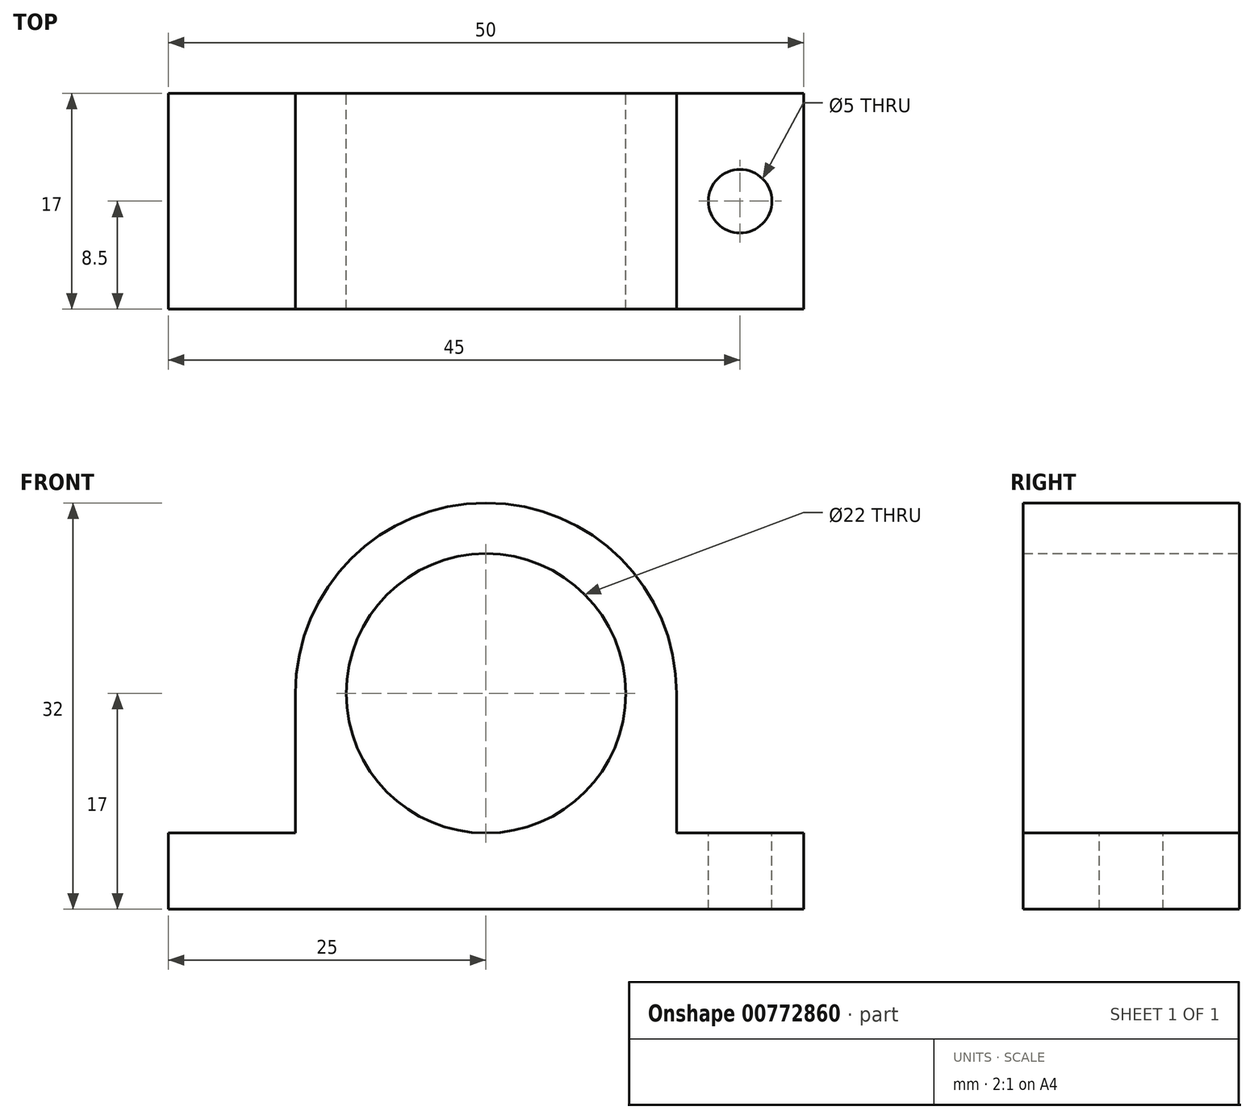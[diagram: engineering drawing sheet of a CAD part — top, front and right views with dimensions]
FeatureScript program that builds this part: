
annotation { "Feature Type Name" : "Feature", "Feature Type Description" : "" }
export const myFeature = defineFeature(function(context is Context, id is Id, definition is map)
    precondition{}
    {
        {
            var Q0;
            Q0=qCreatedBy(makeId("Front.planeOp"),FACE);
            var sketch = newSketch(context, id + "F0", { "sketchPlane" : qUnion([Q0])});
            skCircle(sketch, "E0", {"center": v(0, 0) * mm, "radius": 11 * mm});
            skCircle(sketch, "E1", {"center": v(0, 0) * mm, "radius": 15 * mm});
            skLineSegment(sketch, "E2", {"start": v(-15, 0) * mm, "end": v(-15, -11) * mm});
            skLineSegment(sketch, "E3", {"start": v(-15, -11) * mm, "end": v(-25, -11) * mm});
            skLineSegment(sketch, "E4", {"start": v(-25, -11) * mm, "end": v(-25, -17) * mm});
            skLineSegment(sketch, "E5.MirrorCS", {"start": v(15, 0) * mm, "end": v(15, -11) * mm});
            skLineSegment(sketch, "E6.MirrorCS", {"start": v(15, -11) * mm, "end": v(25, -11) * mm});
            skLineSegment(sketch, "E7.MirrorCS", {"start": v(25, -11) * mm, "end": v(25, -17) * mm});
            skLineSegment(sketch, "E8", {"start": v(-25, -17) * mm, "end": v(25, -17) * mm});
            skSolve(sketch);
        }
        {
            var Q0;
            Q0=makeQuery(id+"F0.imprint","IMPRINT",FACE,{"disambiguationData":[TD([[makeQuery(id+"F0.imprint","IMPRINT",EDGE,{"derivedFrom":sQuery(id+"F0.wireOp",EDGE,"E0")}),-1.0]])]});
            var Q1;
            {var subQ0=sQuery(id+"F0.wireOp",EDGE,"E2");Q1=makeQuery(id+"F0.imprint","IMPRINT",FACE,{"disambiguationData":[TD([[makeQuery(id+"F0.imprint","IMPRINT",EDGE,{"derivedFrom":subQ0}),1.0]])]});}
            extrude(context, id + "F1", {"entities" : qUnion([Q0, Q1]), "depth" : 17 * mm, "offsetDistance" : 25 * mm});
        }
        {
            var Q0;
            Q0=makeQuery(id+"F1.opExtrude","SWEPT_FACE",FACE,{"disambiguationData":[OSD([sQuery(id+"F0.wireOp",EDGE,"E6.MirrorCS")])]});
            var sketch = newSketch(context, id + "F2", { "sketchPlane" : qUnion([Q0])});
            skCircle(sketch, "E9", {"center": v(20, -8.5) * mm, "radius": 2.5 * mm});
            skCircle(sketch, "E10.MirrorC", {"center": v(-20, -8.5) * mm, "radius": 2.5 * mm});
            skSolve(sketch);
        }
        {
            var Q0;
            Q0=makeQuery(id+"F2.imprint","IMPRINT",FACE,{"disambiguationData":[TD([[makeQuery(id+"F2.imprint","IMPRINT",EDGE,{"derivedFrom":sQuery(id+"F2.wireOp",EDGE,"E10.MirrorC")}),-1.0]])]});
            var Q1;
            Q1=makeQuery(id+"F2.imprint","IMPRINT",FACE,{"disambiguationData":[TD([[makeQuery(id+"F2.imprint","IMPRINT",EDGE,{"derivedFrom":sQuery(id+"F2.wireOp",EDGE,"E9")}),1.0]])]});
            extrude(context, id + "F3", {"entities" : qUnion([Q0, Q1]), "operationType" : NewBodyOperationType.REMOVE, "endBound" : BoundingType.THROUGH_ALL, "oppositeDirection" : true, "depth" : 25 * mm, "offsetDistance" : 25 * mm});
        }
    });
